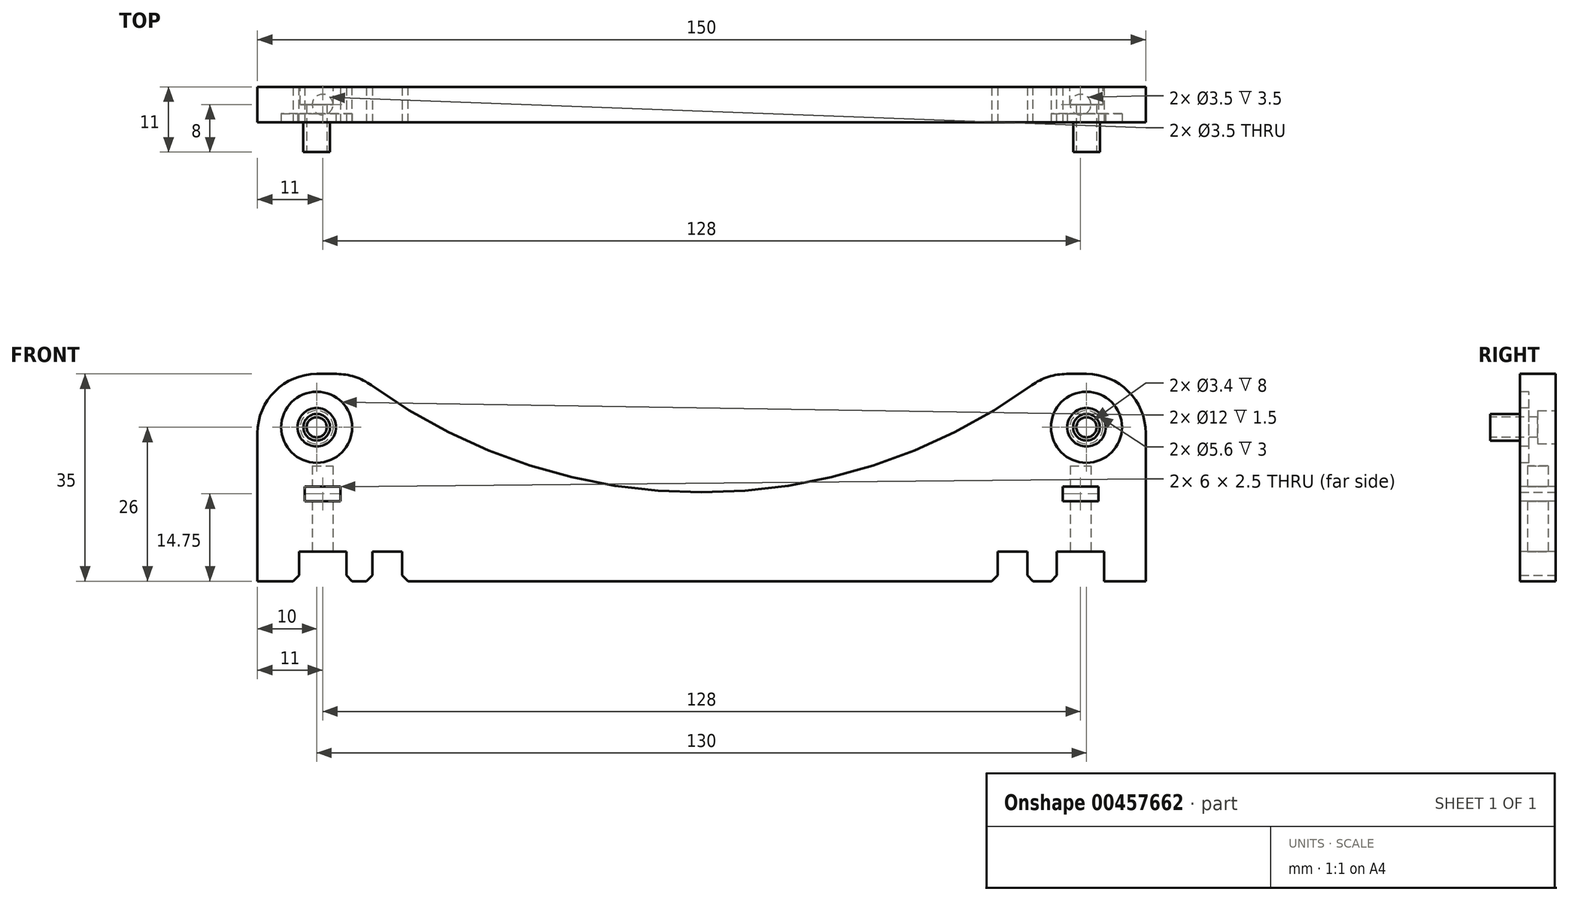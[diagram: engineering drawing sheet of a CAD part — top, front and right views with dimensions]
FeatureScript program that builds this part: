
annotation { "Feature Type Name" : "Feature", "Feature Type Description" : "" }
export const myFeature = defineFeature(function(context is Context, id is Id, definition is map)
    precondition{}
    {
        {
            var Q0;
            Q0=qCreatedBy(makeId("Front.planeOp"),FACE);
            var sketch = newSketch(context, id + "F0", { "sketchPlane" : qUnion([Q0])});
            skLineSegment(sketch, "E0.bottom", {"start": v(75, 0) * mm, "end": v(-75, 0) * mm});
            skLineSegment(sketch, "E0.top", {"start": v(75, 35) * mm, "end": v(-75, 35) * mm});
            skLineSegment(sketch, "E0.left", {"start": v(75, 0) * mm, "end": v(75, 35) * mm});
            skLineSegment(sketch, "E0.right", {"start": v(-75, 0) * mm, "end": v(-75, 35) * mm});
            skPoint(sketch, "E0.middle", {"position": v(0, 10) * mm});
            skCircle(sketch, "E1", {"center": v(0, 110) * mm, "radius": 100 * mm, "construction": true});
            skCircle(sketch, "E2", {"center": v(0, 110) * mm, "radius": 95 * mm});
            skSolve(sketch);
        }
        {
            var Q0;
            Q0=makeQuery(id+"F0.imprint","IMPRINT",FACE,{"disambiguationData":[TD([[makeQuery(id+"F0.imprint","IMPRINT",EDGE,{"derivedFrom":sQuery(id+"F0.wireOp",EDGE,"E0.bottom")}),-1.0]])]});
            extrude(context, id + "F1", {"entities" : qUnion([Q0]), "depth" : 6 * mm});
        }
        {
            var Q0;
            Q0=makeQuery(id+"F1.opExtrude","CAP_FACE",FACE,{"disambiguationData":[OSD([sQuery(id+"F0.wireOp",EDGE,"E0.bottom"),sQuery(id+"F0.wireOp",EDGE,"E0.top"),sQuery(id+"F0.wireOp",EDGE,"E0.left"),sQuery(id+"F0.wireOp",EDGE,"E0.right"),sQuery(id+"F0.wireOp",EDGE,"E2")])],"isStart":false});
            var sketch = newSketch(context, id + "F2", { "sketchPlane" : qUnion([Q0])});
            skCircle(sketch, "E3", {"center": v(0, 110) * mm, "radius": 100 * mm, "construction": true});
            skCircle(sketch, "E4", {"center": v(-65, 26) * mm, "radius": 6 * mm});
            skCircle(sketch, "E5", {"center": v(65, 26) * mm, "radius": 6 * mm});
            skCircle(sketch, "E6", {"center": v(-65, 26) * mm, "radius": 3.25 * mm});
            skCircle(sketch, "E7", {"center": v(65, 26) * mm, "radius": 3.25 * mm});
            skSolve(sketch);
        }
        {
            var Q0;
            Q0=makeQuery(id+"F2.imprint","IMPRINT",FACE,{"disambiguationData":[TD([[makeQuery(id+"F2.imprint","IMPRINT",EDGE,{"derivedFrom":sQuery(id+"F2.wireOp",EDGE,"E4")}),1.0]])]});
            var Q1;
            Q1=makeQuery(id+"F2.imprint","IMPRINT",FACE,{"disambiguationData":[TD([[makeQuery(id+"F2.imprint","IMPRINT",EDGE,{"derivedFrom":sQuery(id+"F2.wireOp",EDGE,"E5")}),1.0]])]});
            extrude(context, id + "F3", {"entities" : qUnion([Q0, Q1]), "operationType" : NewBodyOperationType.REMOVE, "oppositeDirection" : true, "depth" : 1.5 * mm});
        }
        {
            var Q0;
            {var subQ0=sQuery(id+"F0.wireOp",EDGE,"E0.right");var subQ1=sQuery(id+"F0.wireOp",EDGE,"E0.top");var subQ2=sQuery(id+"F0.wireOp",EDGE,"E2");var subQ3=sQuery(id+"F0.wireOp",EDGE,"E0.left");var subQ4=sQuery(id+"F0.wireOp",EDGE,"E0.bottom");Q0=makeQuery(id+"F3.boolean.opBoolean","SPLIT",FACE,{"disambiguationData":[TD([makeQuery(id+"F1.opExtrude","SWEPT_FACE",FACE,{"disambiguationData":[OSD([subQ4])]})])],"derivedFrom":makeQuery(id+"F1.opExtrude","CAP_FACE",FACE,{"disambiguationData":[OSD([subQ4,subQ1,subQ3,subQ0,subQ2])],"isStart":false})});}
            var sketch = newSketch(context, id + "F4", { "sketchPlane" : qUnion([Q0])});
            skLineSegment(sketch, "E8.bottom", {"start": v(-68, 0) * mm, "end": v(-60, 0) * mm});
            skLineSegment(sketch, "E8.top", {"start": v(-68, 5) * mm, "end": v(-60, 5) * mm});
            skLineSegment(sketch, "E8.left", {"start": v(-68, 0) * mm, "end": v(-68, 5) * mm});
            skLineSegment(sketch, "E8.right", {"start": v(-60, 0) * mm, "end": v(-60, 5) * mm});
            skLineSegment(sketch, "E9.bottom", {"start": v(60, 0) * mm, "end": v(68, 0) * mm});
            skLineSegment(sketch, "E9.top", {"start": v(60, 5) * mm, "end": v(68, 5) * mm});
            skLineSegment(sketch, "E9.left", {"start": v(60, 0) * mm, "end": v(60, 5) * mm});
            skLineSegment(sketch, "E9.right", {"start": v(68, 0) * mm, "end": v(68, 5) * mm});
            skLineSegment(sketch, "E10.bottom", {"start": v(-67, 13.5) * mm, "end": v(-61, 13.5) * mm});
            skLineSegment(sketch, "E10.top", {"start": v(-67, 16) * mm, "end": v(-61, 16) * mm});
            skLineSegment(sketch, "E10.left", {"start": v(-67, 13.5) * mm, "end": v(-67, 16) * mm});
            skLineSegment(sketch, "E10.right", {"start": v(-61, 13.5) * mm, "end": v(-61, 16) * mm});
            skLineSegment(sketch, "E11.bottom", {"start": v(61, 16) * mm, "end": v(67, 16) * mm});
            skLineSegment(sketch, "E11.top", {"start": v(61, 13.5) * mm, "end": v(67, 13.5) * mm});
            skLineSegment(sketch, "E11.left", {"start": v(61, 16) * mm, "end": v(61, 13.5) * mm});
            skLineSegment(sketch, "E11.right", {"start": v(67, 16) * mm, "end": v(67, 13.5) * mm});
            skLineSegment(sketch, "E12.bottom", {"start": v(-55.59, 5) * mm, "end": v(-50.59, 5) * mm});
            skLineSegment(sketch, "E12.top", {"start": v(-55.59, 0) * mm, "end": v(-50.59, 0) * mm});
            skLineSegment(sketch, "E12.left", {"start": v(-55.59, 5) * mm, "end": v(-55.59, 0) * mm});
            skLineSegment(sketch, "E12.right", {"start": v(-50.59, 5) * mm, "end": v(-50.59, 0) * mm});
            skLineSegment(sketch, "E13.bottom", {"start": v(55, 0) * mm, "end": v(50, 0) * mm});
            skLineSegment(sketch, "E13.top", {"start": v(55, 5) * mm, "end": v(50, 5) * mm});
            skLineSegment(sketch, "E13.left", {"start": v(55, 0) * mm, "end": v(55, 5) * mm});
            skLineSegment(sketch, "E13.right", {"start": v(50, 0) * mm, "end": v(50, 5) * mm});
            skSolve(sketch);
        }
        {
            var Q0;
            Q0=makeQuery(id+"F4.imprint","IMPRINT",FACE,{"disambiguationData":[TD([[makeQuery(id+"F4.imprint","IMPRINT",EDGE,{"derivedFrom":sQuery(id+"F4.wireOp",EDGE,"E8.bottom")}),-1.0]])]});
            var Q1;
            Q1=makeQuery(id+"F4.imprint","IMPRINT",FACE,{"disambiguationData":[TD([[makeQuery(id+"F4.imprint","IMPRINT",EDGE,{"derivedFrom":sQuery(id+"F4.wireOp",EDGE,"E9.bottom")}),-1.0]])]});
            var Q2;
            Q2=makeQuery(id+"F4.imprint","IMPRINT",FACE,{"disambiguationData":[TD([[makeQuery(id+"F4.imprint","IMPRINT",EDGE,{"derivedFrom":sQuery(id+"F4.wireOp",EDGE,"E10.bottom")}),1.0]])]});
            var Q3;
            Q3=makeQuery(id+"F4.imprint","IMPRINT",FACE,{"disambiguationData":[TD([[makeQuery(id+"F4.imprint","IMPRINT",EDGE,{"derivedFrom":sQuery(id+"F4.wireOp",EDGE,"E11.bottom")}),-1.0]])]});
            var Q4;
            Q4=makeQuery(id+"F4.imprint","IMPRINT",FACE,{"disambiguationData":[TD([[makeQuery(id+"F4.imprint","IMPRINT",EDGE,{"derivedFrom":sQuery(id+"F4.wireOp",EDGE,"E13.bottom")}),-1.0]])]});
            var Q5;
            Q5=makeQuery(id+"F4.imprint","IMPRINT",FACE,{"disambiguationData":[TD([[makeQuery(id+"F4.imprint","IMPRINT",EDGE,{"derivedFrom":sQuery(id+"F4.wireOp",EDGE,"E12.bottom")}),-1.0]])]});
            extrude(context, id + "F5", {"entities" : qUnion([Q0, Q1, Q2, Q3, Q4, Q5]), "operationType" : NewBodyOperationType.REMOVE, "endBound" : BoundingType.THROUGH_ALL, "oppositeDirection" : true, "depth" : 25 * mm});
        }
        {
            var Q0;
            Q0=makeQuery(id+"F1.opExtrude","SWEPT_EDGE",EDGE,{"disambiguationData":[OSD([sQuery(id+"F0.wireOp",EDGE,"E0.top"),sQuery(id+"F0.wireOp",EDGE,"E0.right")])]});
            var Q1;
            Q1=makeQuery(id+"F1.opExtrude","SWEPT_EDGE",EDGE,{"disambiguationData":[OSD([sQuery(id+"F0.wireOp",EDGE,"E0.top"),sQuery(id+"F0.wireOp",EDGE,"E0.left")])]});
            var Q2;
            {var subQ0=sQuery(id+"F0.wireOp",EDGE,"E2");var subQ1=sQuery(id+"F0.wireOp",EDGE,"E0.top");Q2=makeQuery(id+"F1.opExtrude","SWEPT_EDGE",EDGE,{"disambiguationData":[OSD([subQ1,subQ0]),TDD([makeQuery(id+"F0.imprint","INTERSECT",VERTEX,{"disambiguationData":[OD(0.0)],"derivedFrom":[subQ1,subQ0]})])]});}
            var Q3;
            {var subQ0=sQuery(id+"F0.wireOp",EDGE,"E2");var subQ1=sQuery(id+"F0.wireOp",EDGE,"E0.top");Q3=makeQuery(id+"F1.opExtrude","SWEPT_EDGE",EDGE,{"disambiguationData":[OSD([subQ1,subQ0]),TDD([makeQuery(id+"F0.imprint","INTERSECT",VERTEX,{"disambiguationData":[OD(1.0)],"derivedFrom":[subQ1,subQ0]})])]});}
            fillet(context, id + "F6", {"entities" : qUnion([Q0, Q1, Q2, Q3]), "radius" : 10 * mm, "tangentPropagation" : true, "allowEdgeOverflow" : false});
        }
        {
            var Q0;
            Q0=makeQuery(id+"F5.boolean.opBoolean","COPY",EDGE,{"derivedFrom":makeQuery(id+"F5.opExtrude","SWEPT_EDGE",EDGE,{"disambiguationData":[OSD([sQuery(id+"F0.wireOp",EDGE,"E0.bottom"),sQuery(id+"F4.wireOp",EDGE,"E8.bottom"),sQuery(id+"F4.wireOp",EDGE,"E8.left")])]})});
            var Q1;
            Q1=makeQuery(id+"F5.boolean.opBoolean","COPY",EDGE,{"derivedFrom":makeQuery(id+"F5.opExtrude","SWEPT_EDGE",EDGE,{"disambiguationData":[OSD([sQuery(id+"F0.wireOp",EDGE,"E0.bottom"),sQuery(id+"F4.wireOp",EDGE,"E8.bottom"),sQuery(id+"F4.wireOp",EDGE,"E8.right")])]})});
            var Q2;
            Q2=makeQuery(id+"F5.boolean.opBoolean","COPY",EDGE,{"derivedFrom":makeQuery(id+"F5.opExtrude","SWEPT_EDGE",EDGE,{"disambiguationData":[OSD([sQuery(id+"F0.wireOp",EDGE,"E0.bottom"),sQuery(id+"F4.wireOp",EDGE,"E9.bottom"),sQuery(id+"F4.wireOp",EDGE,"E9.left")])]})});
            var Q3;
            Q3=makeQuery(id+"F5.boolean.opBoolean","COPY",EDGE,{"derivedFrom":makeQuery(id+"F5.opExtrude","SWEPT_EDGE",EDGE,{"disambiguationData":[OSD([sQuery(id+"F0.wireOp",EDGE,"E0.bottom"),sQuery(id+"F4.wireOp",EDGE,"E9.bottom"),sQuery(id+"F4.wireOp",EDGE,"E9.right")])]})});
            var Q4;
            Q4=makeQuery(id+"F5.boolean.opBoolean","COPY",EDGE,{"derivedFrom":makeQuery(id+"F5.opExtrude","SWEPT_EDGE",EDGE,{"disambiguationData":[OSD([sQuery(id+"F0.wireOp",EDGE,"E0.bottom"),sQuery(id+"F4.wireOp",EDGE,"E12.top"),sQuery(id+"F4.wireOp",EDGE,"E12.left")])]})});
            var Q5;
            Q5=makeQuery(id+"F5.boolean.opBoolean","COPY",EDGE,{"derivedFrom":makeQuery(id+"F5.opExtrude","SWEPT_EDGE",EDGE,{"disambiguationData":[OSD([sQuery(id+"F0.wireOp",EDGE,"E0.bottom"),sQuery(id+"F4.wireOp",EDGE,"E12.top"),sQuery(id+"F4.wireOp",EDGE,"E12.right")])]})});
            var Q6;
            Q6=makeQuery(id+"F5.boolean.opBoolean","COPY",EDGE,{"derivedFrom":makeQuery(id+"F5.opExtrude","SWEPT_EDGE",EDGE,{"disambiguationData":[OSD([sQuery(id+"F0.wireOp",EDGE,"E0.bottom"),sQuery(id+"F4.wireOp",EDGE,"E13.bottom"),sQuery(id+"F4.wireOp",EDGE,"E13.right")])]})});
            var Q7;
            Q7=makeQuery(id+"F5.boolean.opBoolean","COPY",EDGE,{"derivedFrom":makeQuery(id+"F5.opExtrude","SWEPT_EDGE",EDGE,{"disambiguationData":[OSD([sQuery(id+"F0.wireOp",EDGE,"E0.bottom"),sQuery(id+"F4.wireOp",EDGE,"E13.bottom"),sQuery(id+"F4.wireOp",EDGE,"E13.left")])]})});
            chamfer(context, id + "F7", {"entities" : qUnion([Q0, Q1, Q2, Q3, Q4, Q5, Q6, Q7]), "width" : 1 * mm, "tangentPropagation" : true});
        }
        {
            var Q0;
            Q0=makeQuery(id+"F5.boolean.opBoolean","COPY",FACE,{"derivedFrom":makeQuery(id+"F5.opExtrude","SWEPT_FACE",FACE,{"disambiguationData":[OSD([sQuery(id+"F4.wireOp",EDGE,"E8.top")])]})});
            var sketch = newSketch(context, id + "F8", { "sketchPlane" : qUnion([Q0])});
            skCircle(sketch, "E14", {"center": v(-64, 3) * mm, "radius": 1.75 * mm});
            skSolve(sketch);
        }
        {
            var Q0;
            Q0=makeQuery(id+"F8.imprint","IMPRINT",FACE,{"disambiguationData":[TD([[makeQuery(id+"F8.imprint","IMPRINT",EDGE,{"derivedFrom":sQuery(id+"F8.wireOp",EDGE,"E14")}),1.0]])]});
            extrude(context, id + "F9", {"entities" : qUnion([Q0]), "operationType" : NewBodyOperationType.REMOVE, "oppositeDirection" : true, "depth" : 14.5 * mm});
        }
        {
            var Q0;
            Q0=makeQuery(id+"F5.boolean.opBoolean","COPY",FACE,{"derivedFrom":makeQuery(id+"F5.opExtrude","SWEPT_FACE",FACE,{"disambiguationData":[OSD([sQuery(id+"F4.wireOp",EDGE,"E9.top")])]})});
            var sketch = newSketch(context, id + "F10", { "sketchPlane" : qUnion([Q0])});
            skCircle(sketch, "E15", {"center": v(64, 3) * mm, "radius": 1.75 * mm});
            skSolve(sketch);
        }
        {
            var Q0;
            Q0=makeQuery(id+"F10.imprint","IMPRINT",FACE,{"disambiguationData":[TD([[makeQuery(id+"F10.imprint","IMPRINT",EDGE,{"derivedFrom":sQuery(id+"F10.wireOp",EDGE,"E15")}),1.0]])]});
            extrude(context, id + "F11", {"entities" : qUnion([Q0]), "operationType" : NewBodyOperationType.REMOVE, "oppositeDirection" : true, "depth" : 14.5 * mm});
        }
        {
            var Q0;
            Q0=makeQuery(id+"F3.boolean.opBoolean","SPLIT",FACE,{"disambiguationData":[TD([makeQuery(id+"F3.opExtrude","SWEPT_FACE",FACE,{"disambiguationData":[OSD([sQuery(id+"F2.wireOp",EDGE,"E6")])]})])],"derivedFrom":makeQuery(id+"F1.opExtrude","CAP_FACE",FACE,{"disambiguationData":[OSD([sQuery(id+"F0.wireOp",EDGE,"E0.bottom"),sQuery(id+"F0.wireOp",EDGE,"E0.top"),sQuery(id+"F0.wireOp",EDGE,"E0.left"),sQuery(id+"F0.wireOp",EDGE,"E0.right"),sQuery(id+"F0.wireOp",EDGE,"E2")])],"isStart":false})});
            var sketch = newSketch(context, id + "F12", { "sketchPlane" : qUnion([Q0])});
            skCircle(sketch, "E16", {"center": v(-65, 26) * mm, "radius": 2.25 * mm});
            skSolve(sketch);
        }
        {
            var Q0;
            Q0=makeQuery(id+"F12.imprint","IMPRINT",FACE,{"disambiguationData":[TD([[makeQuery(id+"F12.imprint","IMPRINT",EDGE,{"derivedFrom":sQuery(id+"F12.wireOp",EDGE,"E16")}),1.0]])]});
            extrude(context, id + "F13", {"entities" : qUnion([Q0]), "operationType" : NewBodyOperationType.ADD, "depth" : 5 * mm});
        }
        {
            var Q0;
            Q0=makeQuery(id+"F13.opExtrude","CAP_FACE",FACE,{"disambiguationData":[OSD([sQuery(id+"F12.wireOp",EDGE,"E16")])],"isStart":false});
            var sketch = newSketch(context, id + "F14", { "sketchPlane" : qUnion([Q0])});
            skCircle(sketch, "E17", {"center": v(-65, 26) * mm, "radius": 1.7 * mm});
            skSolve(sketch);
        }
        {
            var Q0;
            Q0=makeQuery(id+"F14.imprint","IMPRINT",FACE,{"disambiguationData":[TD([[makeQuery(id+"F14.imprint","IMPRINT",EDGE,{"derivedFrom":sQuery(id+"F14.wireOp",EDGE,"E17")}),1.0]])]});
            extrude(context, id + "F15", {"entities" : qUnion([Q0]), "operationType" : NewBodyOperationType.REMOVE, "endBound" : BoundingType.THROUGH_ALL, "oppositeDirection" : true, "depth" : 25 * mm});
        }
        {
            var Q0;
            Q0=makeQuery(id+"F3.boolean.opBoolean","SPLIT",FACE,{"disambiguationData":[TD([makeQuery(id+"F3.opExtrude","SWEPT_FACE",FACE,{"disambiguationData":[OSD([sQuery(id+"F2.wireOp",EDGE,"E7")])]})])],"derivedFrom":makeQuery(id+"F1.opExtrude","CAP_FACE",FACE,{"disambiguationData":[OSD([sQuery(id+"F0.wireOp",EDGE,"E0.bottom"),sQuery(id+"F0.wireOp",EDGE,"E0.top"),sQuery(id+"F0.wireOp",EDGE,"E0.left"),sQuery(id+"F0.wireOp",EDGE,"E0.right"),sQuery(id+"F0.wireOp",EDGE,"E2")])],"isStart":false})});
            var sketch = newSketch(context, id + "F16", { "sketchPlane" : qUnion([Q0])});
            skCircle(sketch, "E18", {"center": v(65, 26) * mm, "radius": 2.25 * mm});
            skSolve(sketch);
        }
        {
            var Q0;
            Q0=makeQuery(id+"F16.imprint","IMPRINT",FACE,{"disambiguationData":[TD([[makeQuery(id+"F16.imprint","IMPRINT",EDGE,{"derivedFrom":sQuery(id+"F16.wireOp",EDGE,"E18")}),1.0]])]});
            extrude(context, id + "F17", {"entities" : qUnion([Q0]), "operationType" : NewBodyOperationType.ADD, "depth" : 5 * mm});
        }
        {
            var Q0;
            Q0=makeQuery(id+"F17.opExtrude","CAP_FACE",FACE,{"disambiguationData":[OSD([sQuery(id+"F16.wireOp",EDGE,"E18")])],"isStart":false});
            var sketch = newSketch(context, id + "F18", { "sketchPlane" : qUnion([Q0])});
            skCircle(sketch, "E19", {"center": v(65, 26) * mm, "radius": 1.7 * mm});
            skSolve(sketch);
        }
        {
            var Q0;
            Q0=makeQuery(id+"F18.imprint","IMPRINT",FACE,{"disambiguationData":[TD([[makeQuery(id+"F18.imprint","IMPRINT",EDGE,{"derivedFrom":sQuery(id+"F18.wireOp",EDGE,"E19")}),1.0]])]});
            extrude(context, id + "F19", {"entities" : qUnion([Q0]), "operationType" : NewBodyOperationType.REMOVE, "endBound" : BoundingType.THROUGH_ALL, "oppositeDirection" : true, "depth" : 25 * mm});
        }
        {
            var Q0;
            Q0=makeQuery(id+"F1.opExtrude","CAP_FACE",FACE,{"disambiguationData":[OSD([sQuery(id+"F0.wireOp",EDGE,"E0.bottom"),sQuery(id+"F0.wireOp",EDGE,"E0.top"),sQuery(id+"F0.wireOp",EDGE,"E0.left"),sQuery(id+"F0.wireOp",EDGE,"E0.right"),sQuery(id+"F0.wireOp",EDGE,"E2")])],"isStart":true});
            var sketch = newSketch(context, id + "F20", { "sketchPlane" : qUnion([Q0])});
            skCircle(sketch, "E20", {"center": v(-65, 26) * mm, "radius": 2.8 * mm});
            skCircle(sketch, "E21", {"center": v(65, 26) * mm, "radius": 2.8 * mm});
            skSolve(sketch);
        }
        {
            var Q0;
            Q0=makeQuery(id+"F20.imprint","IMPRINT",FACE,{"disambiguationData":[TD([[makeQuery(id+"F20.imprint","IMPRINT",EDGE,{"derivedFrom":sQuery(id+"F20.wireOp",EDGE,"E20")}),1.0]])]});
            var Q1;
            Q1=makeQuery(id+"F20.imprint","IMPRINT",FACE,{"disambiguationData":[TD([[makeQuery(id+"F20.imprint","IMPRINT",EDGE,{"derivedFrom":sQuery(id+"F20.wireOp",EDGE,"E21")}),1.0]])]});
            extrude(context, id + "F21", {"entities" : qUnion([Q0, Q1]), "operationType" : NewBodyOperationType.REMOVE, "oppositeDirection" : true, "depth" : 3 * mm});
        }
    });
